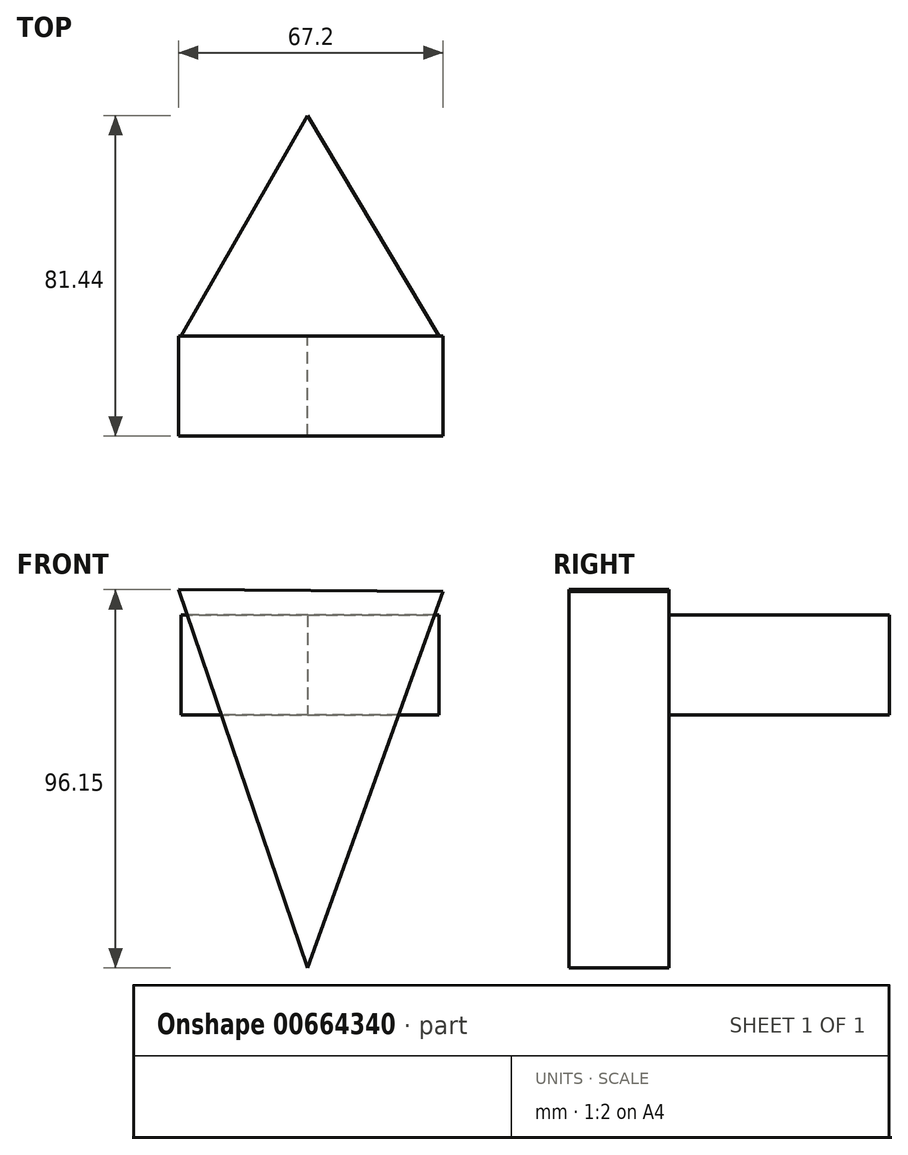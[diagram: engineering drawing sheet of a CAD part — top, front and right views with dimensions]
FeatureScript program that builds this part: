
annotation { "Feature Type Name" : "Feature", "Feature Type Description" : "" }
export const myFeature = defineFeature(function(context is Context, id is Id, definition is map)
    precondition{}
    {
        {
            var Q0;
            Q0=qCreatedBy(makeId("Front.planeOp"),FACE);
            var sketch = newSketch(context, id + "F0", { "sketchPlane" : qUnion([Q0])});
            skLineSegment(sketch, "E0", {"start": v(-32.8, 31.9) * mm, "end": v(0, -64.26) * mm});
            skLineSegment(sketch, "E1", {"start": v(0, -64.26) * mm, "end": v(34.39, 31.34) * mm});
            skLineSegment(sketch, "E2", {"start": v(34.39, 31.34) * mm, "end": v(-32.8, 31.9) * mm});
            skSolve(sketch);
        }
        {
            var Q0;
            Q0=makeQuery(id+"F0.imprint","IMPRINT",FACE,{"disambiguationData":[TD([[makeQuery(id+"F0.imprint","IMPRINT",EDGE,{"derivedFrom":sQuery(id+"F0.wireOp",EDGE,"E0")}),1.0]])]});
            extrude(context, id + "F1", {"entities" : qUnion([Q0]), "depth" : 25.4 * mm, "offsetDistance" : 25.4 * mm});
        }
        {
            var Q0;
            Q0=qCreatedBy(makeId("Top.planeOp"),FACE);
            var sketch = newSketch(context, id + "F2", { "sketchPlane" : qUnion([Q0])});
            skLineSegment(sketch, "E3", {"start": v(-32.2, 0) * mm, "end": v(0, 56.04) * mm});
            skLineSegment(sketch, "E4", {"start": v(0, 56.04) * mm, "end": v(33.34, 0) * mm});
            skLineSegment(sketch, "E5", {"start": v(33.34, 0) * mm, "end": v(-32.2, 0) * mm});
            skSolve(sketch);
        }
        {
            var Q0;
            Q0=makeQuery(id+"F2.imprint","IMPRINT",FACE,{"disambiguationData":[TD([[makeQuery(id+"F2.imprint","IMPRINT",EDGE,{"derivedFrom":sQuery(id+"F2.wireOp",EDGE,"E3")}),-1.0]])]});
            extrude(context, id + "F3", {"entities" : qUnion([Q0]), "operationType" : NewBodyOperationType.ADD, "depth" : 25.4 * mm, "offsetDistance" : 25.4 * mm});
        }
    });
